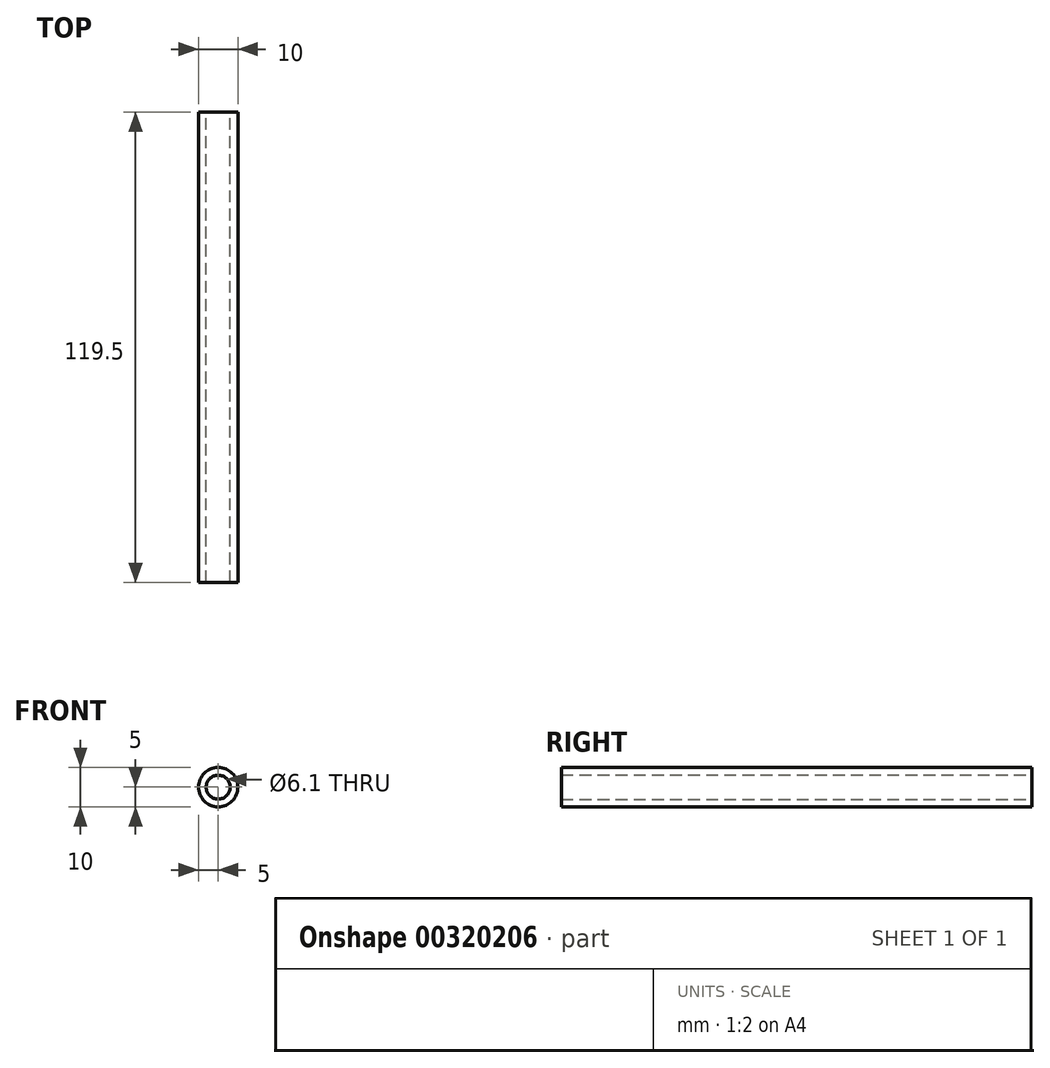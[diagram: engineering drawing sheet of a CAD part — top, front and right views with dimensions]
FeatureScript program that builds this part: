
annotation { "Feature Type Name" : "Feature", "Feature Type Description" : "" }
export const myFeature = defineFeature(function(context is Context, id is Id, definition is map)
    precondition{}
    {
        {
            var Q0;
            Q0=qCreatedBy(makeId("Front.planeOp"),FACE);
            var sketch = newSketch(context, id + "F0", { "sketchPlane" : qUnion([Q0])});
            skCircle(sketch, "E0", {"center": v(0, 0) * mm, "radius": 5 * mm});
            skCircle(sketch, "E1", {"center": v(0, 0) * mm, "radius": 3.05 * mm});
            skSolve(sketch);
        }
        {
            var Q0;
            Q0=qSketchRegion(id+"F0",true);
            extrude(context, id + "F1", {"entities" : qUnion([Q0]), "endBound" : BoundingType.SYMMETRIC, "depth" : 119.5 * mm});
        }
    });
